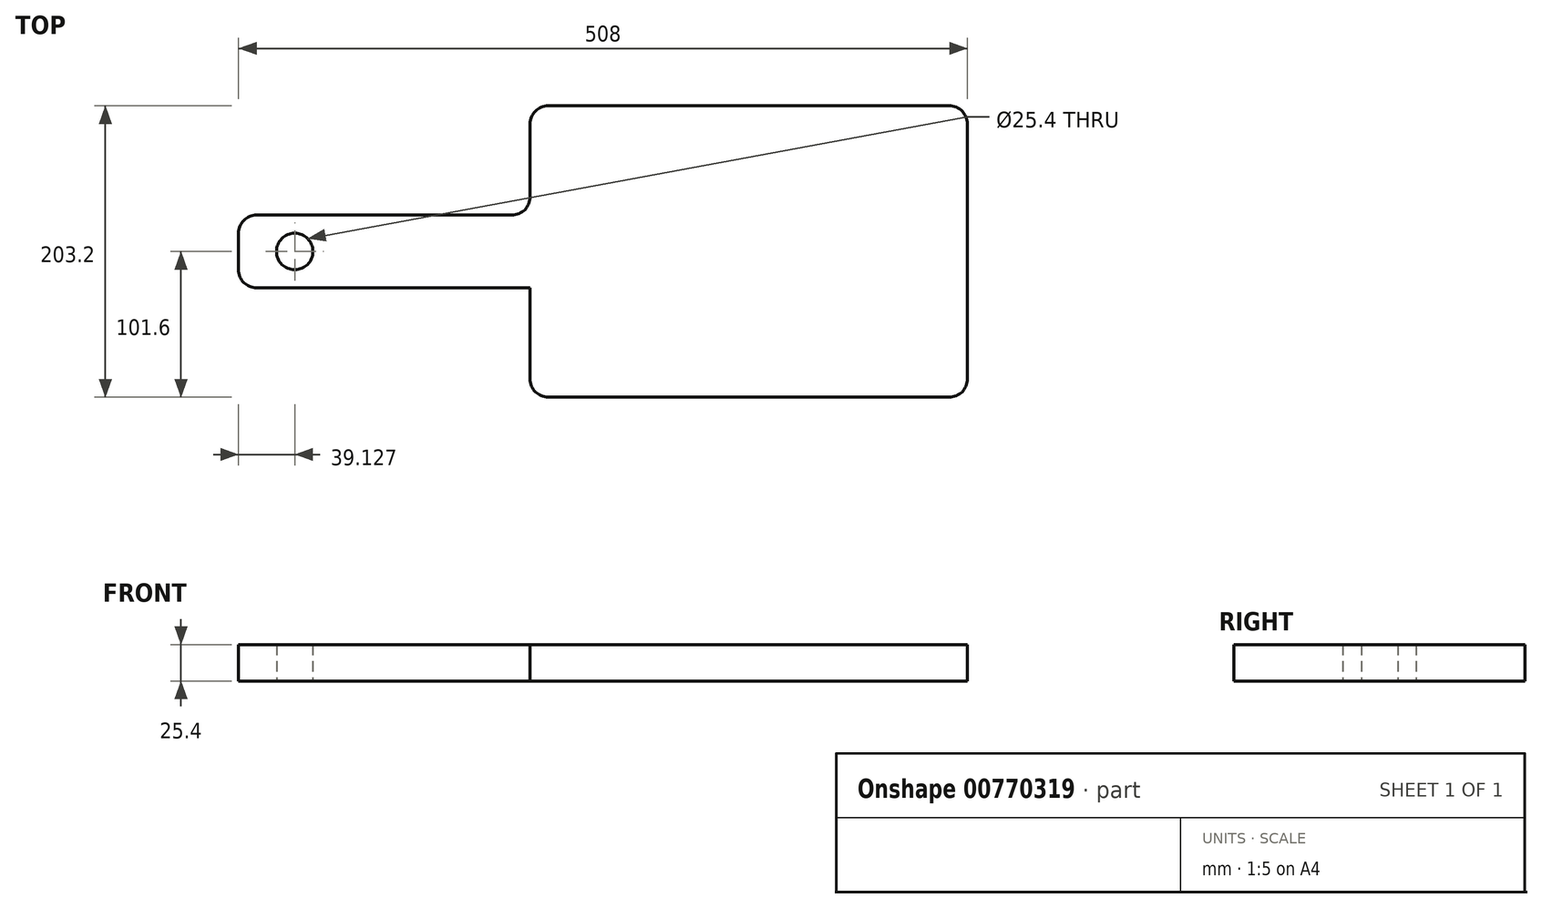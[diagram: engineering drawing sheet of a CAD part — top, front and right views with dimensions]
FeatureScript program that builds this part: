
annotation { "Feature Type Name" : "Feature", "Feature Type Description" : "" }
export const myFeature = defineFeature(function(context is Context, id is Id, definition is map)
    precondition{}
    {
        {
            var Q0;
            Q0=qCreatedBy(makeId("Top.planeOp"),FACE);
            var sketch = newSketch(context, id + "F0", { "sketchPlane" : qUnion([Q0])});
            skLineSegment(sketch, "E0.bottom", {"start": v(0, 0) * mm, "end": v(304.8, 0) * mm});
            skLineSegment(sketch, "E0.top", {"start": v(0, 203.2) * mm, "end": v(304.8, 203.2) * mm});
            skLineSegment(sketch, "E0.left", {"start": v(0, 0) * mm, "end": v(0, 203.2) * mm});
            skLineSegment(sketch, "E0.right", {"start": v(304.8, 0) * mm, "end": v(304.8, 203.2) * mm});
            skLineSegment(sketch, "E1.bottom", {"start": v(0, 127) * mm, "end": v(-203.2, 127) * mm});
            skLineSegment(sketch, "E1.top", {"start": v(0, 76.2) * mm, "end": v(-203.2, 76.2) * mm});
            skLineSegment(sketch, "E1.left", {"start": v(0, 127) * mm, "end": v(0, 76.2) * mm});
            skLineSegment(sketch, "E1.right", {"start": v(-203.2, 127) * mm, "end": v(-203.2, 76.2) * mm});
            skCircle(sketch, "E2", {"center": v(-164.07, 101.6) * mm, "radius": 12.7 * mm});
            skSolve(sketch);
        }
        {
            var Q0;
            Q0 = qSketchRegion(id + "F0", true);
            extrude(context, id + "F1", {"entities" : qUnion([Q0]), "depth" : 25.4 * mm, "offsetDistance" : 25.4 * mm});
        }
        {
            var Q0;
            Q0=makeQuery(id+"F1.opExtrude","SWEPT_EDGE",EDGE,{"disambiguationData":[OSD([sQuery(id+"F0.wireOp",EDGE,"E0.left"),sQuery(id+"F0.wireOp",EDGE,"E1.bottom"),sQuery(id+"F0.wireOp",EDGE,"E1.left")])]});
            var Q1;
            Q1=makeQuery(id+"F1.opExtrude","SWEPT_EDGE",EDGE,{"disambiguationData":[OSD([sQuery(id+"F0.wireOp",EDGE,"E1.bottom"),sQuery(id+"F0.wireOp",EDGE,"E1.right")])]});
            var Q2;
            Q2=makeQuery(id+"F1.opExtrude","SWEPT_EDGE",EDGE,{"disambiguationData":[OSD([sQuery(id+"F0.wireOp",EDGE,"E1.top"),sQuery(id+"F0.wireOp",EDGE,"E1.right")])]});
            fillet(context, id + "F2", {"entities" : qUnion([Q0, Q1, Q2]), "radius" : 12.7 * mm, "tangentPropagation" : true, "allowEdgeOverflow" : false});
        }
        {
            var Q0;
            Q0=makeQuery(id+"F1.opExtrude","SWEPT_EDGE",EDGE,{"disambiguationData":[OSD([sQuery(id+"F0.wireOp",EDGE,"E0.top"),sQuery(id+"F0.wireOp",EDGE,"E0.left")])]});
            var Q1;
            Q1=makeQuery(id+"F1.opExtrude","SWEPT_EDGE",EDGE,{"disambiguationData":[OSD([sQuery(id+"F0.wireOp",EDGE,"E0.top"),sQuery(id+"F0.wireOp",EDGE,"E0.right")])]});
            var Q2;
            Q2=makeQuery(id+"F1.opExtrude","SWEPT_EDGE",EDGE,{"disambiguationData":[OSD([sQuery(id+"F0.wireOp",EDGE,"E0.bottom"),sQuery(id+"F0.wireOp",EDGE,"E0.right")])]});
            var Q3;
            Q3=makeQuery(id+"F1.opExtrude","SWEPT_EDGE",EDGE,{"disambiguationData":[OSD([sQuery(id+"F0.wireOp",EDGE,"E0.bottom"),sQuery(id+"F0.wireOp",EDGE,"E0.left")])]});
            fillet(context, id + "F3", {"entities" : qUnion([Q0, Q1, Q2, Q3]), "radius" : 12.7 * mm, "tangentPropagation" : true, "allowEdgeOverflow" : false});
        }
    });
